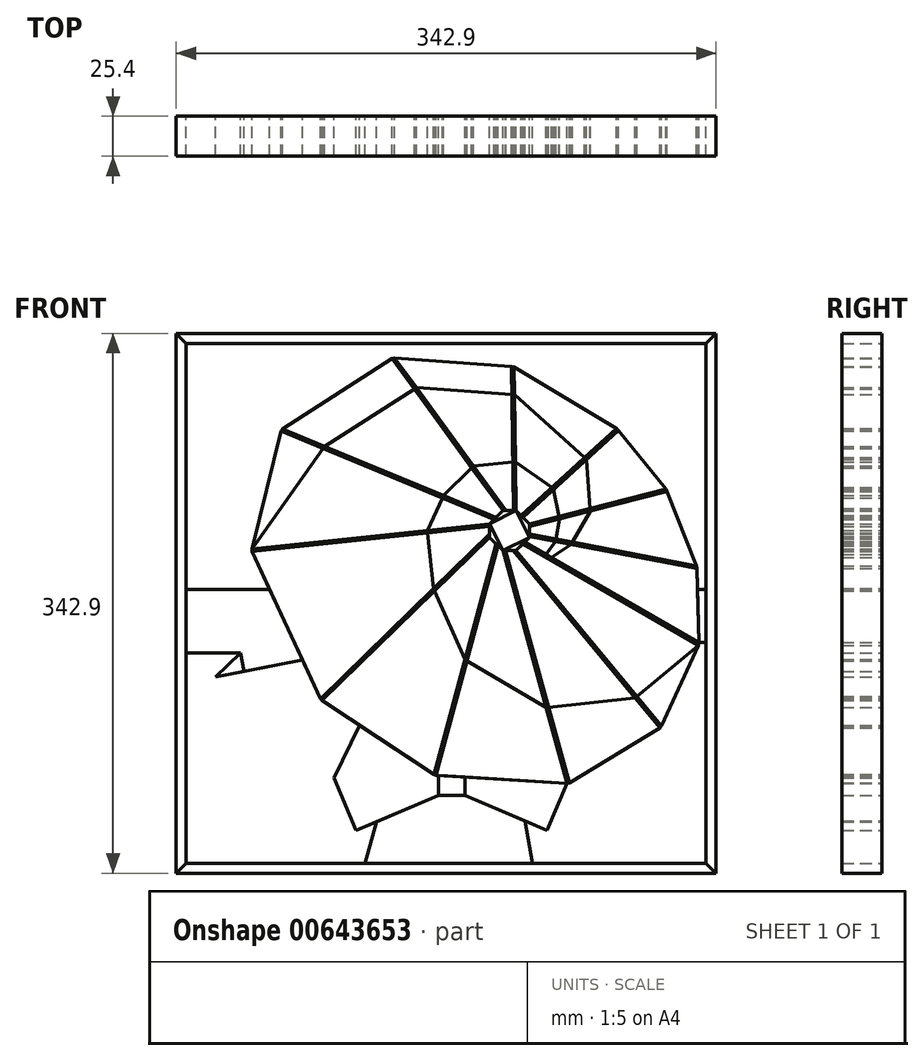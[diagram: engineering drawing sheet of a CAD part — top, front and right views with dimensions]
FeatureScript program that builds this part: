
annotation { "Feature Type Name" : "Feature", "Feature Type Description" : "" }
export const myFeature = defineFeature(function(context is Context, id is Id, definition is map)
    precondition{}
    {
        {
            var Q0;
            Q0=qCreatedBy(makeId("Front.planeOp"),FACE);
            var sketch = newSketch(context, id + "F0", { "sketchPlane" : qUnion([Q0])});
            skLineSegment(sketch, "E0.bottom", {"start": v(-171.45, 171.45) * mm, "end": v(171.45, 171.45) * mm});
            skLineSegment(sketch, "E0.top", {"start": v(-171.45, -171.45) * mm, "end": v(171.45, -171.45) * mm});
            skLineSegment(sketch, "E0.left", {"start": v(-171.45, 171.45) * mm, "end": v(-171.45, -171.45) * mm});
            skLineSegment(sketch, "E0.right", {"start": v(171.45, 171.45) * mm, "end": v(171.45, -171.45) * mm});
            skPoint(sketch, "E0.middle", {"position": v(0, 0) * mm});
            skEllipse(sketch, "E1", {"center": v(19.18, 20.15) * mm, "majorRadius": 153.05 * mm, "minorRadius": 127.05 * mm, "majorAxis": v(0.77, -0.64), "construction": true});
            skLineSegment(sketch, "E2", {"start": v(-55.07, -77.44) * mm, "end": v(-71.28, -110.8) * mm});
            skLineSegment(sketch, "E3", {"start": v(-71.28, -110.8) * mm, "end": v(-57.16, -144.18) * mm});
            skLineSegment(sketch, "E4", {"start": v(-57.16, -144.18) * mm, "end": v(-4.94, -122.09) * mm});
            skLineSegment(sketch, "E5", {"start": v(-4.94, -122.09) * mm, "end": v(-4.94, -109.66) * mm});
            skLineSegment(sketch, "E6", {"start": v(-4.94, -122.09) * mm, "end": v(11.84, -122.09) * mm});
            skLineSegment(sketch, "E7", {"start": v(11.84, -122.09) * mm, "end": v(11.84, -114.36) * mm});
            skLineSegment(sketch, "E8", {"start": v(11.84, -122.09) * mm, "end": v(64.05, -144.18) * mm});
            skLineSegment(sketch, "E9", {"start": v(64.05, -144.18) * mm, "end": v(76.64, -114.43) * mm});
            skLineSegment(sketch, "E10", {"start": v(-171.45, -34.2) * mm, "end": v(-136.3, -34.2) * mm});
            skLineSegment(sketch, "E11", {"start": v(-136.3, -34.2) * mm, "end": v(-152.24, -49.39) * mm});
            skLineSegment(sketch, "E12", {"start": v(-152.24, -49.39) * mm, "end": v(-97.01, -38.77) * mm});
            skLineSegment(sketch, "E13", {"start": v(-136.3, -34.2) * mm, "end": v(-134.05, -45.89) * mm});
            skLineSegment(sketch, "E14", {"start": v(159.43, -30.92) * mm, "end": v(171.45, -30.92) * mm});
            skLineSegment(sketch, "E15", {"start": v(-171.45, 6.09) * mm, "end": v(-118.09, 6.09) * mm});
            skLineSegment(sketch, "E16", {"start": v(171.45, 6.09) * mm, "end": v(161.71, 6.09) * mm});
            skPoint(sketch, "E17.endSnap0", {"position": v(-64.22, -127.5) * mm});
            skLineSegment(sketch, "E18", {"start": v(-44.24, -138.72) * mm, "end": v(-53.12, -171.45) * mm});
            skLineSegment(sketch, "E19", {"start": v(50.01, -138.24) * mm, "end": v(55.89, -171.45) * mm});
            skLineSegment(sketch, "E20.bottom", {"start": v(44.47, 33.4) * mm, "end": v(36, 33.4) * mm});
            skLineSegment(sketch, "E20.top", {"start": v(44.47, 58.8) * mm, "end": v(36, 58.8) * mm});
            skLineSegment(sketch, "E20.left", {"start": v(52.93, 41.87) * mm, "end": v(52.93, 50.33) * mm});
            skLineSegment(sketch, "E20.right", {"start": v(27.53, 41.87) * mm, "end": v(27.53, 50.33) * mm});
            skPoint(sketch, "E20.middle", {"position": v(41.77, 46.48) * mm});
            skLineSegment(sketch, "E21", {"start": v(44.47, 58.8) * mm, "end": v(43.1, 150.02) * mm});
            skLineSegment(sketch, "E22", {"start": v(52.93, 42.42) * mm, "end": v(159.45, 22) * mm});
            skLineSegment(sketch, "E23", {"start": v(44.47, 33.4) * mm, "end": v(136.73, -77.86) * mm});
            skLineSegment(sketch, "E24.0", {"start": v(52.93, 50.33) * mm, "end": v(139.57, 72.45) * mm});
            skLineSegment(sketch, "E25", {"start": v(27.53, 41.87) * mm, "end": v(36, 33.4) * mm});
            skLineSegment(sketch, "E26", {"start": v(27.53, 50.33) * mm, "end": v(36, 58.8) * mm});
            skLineSegment(sketch, "E27", {"start": v(44.47, 58.8) * mm, "end": v(52.93, 50.33) * mm});
            skLineSegment(sketch, "E28", {"start": v(52.93, 41.87) * mm, "end": v(44.47, 33.4) * mm});
            skLineSegment(sketch, "E29.0", {"start": v(52.93, 44.04) * mm, "end": v(159.1, 23.68) * mm});
            skLineSegment(sketch, "E30.0", {"start": v(52.93, 48.7) * mm, "end": v(140.42, 71.02) * mm});
            skPoint(sketch, "E31", {"position": v(48.7, 54.57) * mm});
            skLineSegment(sketch, "E32", {"start": v(36, 33.4) * mm, "end": v(76.64, -114.43) * mm});
            skLineSegment(sketch, "E33", {"start": v(37.65, 33.4) * mm, "end": v(78.18, -114.05) * mm});
            skLineSegment(sketch, "E34", {"start": v(76.64, -114.43) * mm, "end": v(78.18, -114.05) * mm});
            skPoint(sketch, "E35.orphan", {"position": v(78.29, -114.43) * mm});
            skLineSegment(sketch, "E36", {"start": v(42.4, 33.4) * mm, "end": v(135.68, -79.1) * mm});
            skLineSegment(sketch, "E37", {"start": v(135.68, -79.1) * mm, "end": v(136.73, -77.86) * mm});
            skPoint(sketch, "E38", {"position": v(31.77, 37.63) * mm});
            skPoint(sketch, "E39", {"position": v(31.77, 54.57) * mm});
            skPoint(sketch, "E40", {"position": v(48.7, 37.63) * mm});
            skLineSegment(sketch, "E41", {"start": v(27.53, 41.87) * mm, "end": v(-78.73, -61.81) * mm});
            skLineSegment(sketch, "E42", {"start": v(27.53, 44.09) * mm, "end": v(-79.8, -60.65) * mm});
            skLineSegment(sketch, "E43", {"start": v(-79.8, -60.65) * mm, "end": v(-78.73, -61.81) * mm});
            skLineSegment(sketch, "E44", {"start": v(27.53, 50.33) * mm, "end": v(-123.4, 34.61) * mm});
            skLineSegment(sketch, "E45", {"start": v(27.53, 48.74) * mm, "end": v(-123.25, 33.03) * mm});
            skLineSegment(sketch, "E46", {"start": v(-123.25, 33.03) * mm, "end": v(-123.4, 34.61) * mm});
            skLineSegment(sketch, "E47", {"start": v(36, 58.8) * mm, "end": v(-34.43, 155.6) * mm});
            skLineSegment(sketch, "E48", {"start": v(37.96, 58.8) * mm, "end": v(-32.71, 155.94) * mm});
            skLineSegment(sketch, "E49", {"start": v(-32.71, 155.94) * mm, "end": v(-34.43, 155.6) * mm});
            skLineSegment(sketch, "E50", {"start": v(42.88, 58.8) * mm, "end": v(41.5, 150.55) * mm});
            skLineSegment(sketch, "E51", {"start": v(41.5, 150.55) * mm, "end": v(43.1, 150.02) * mm});
            skLineSegment(sketch, "E52", {"start": v(139.57, 72.45) * mm, "end": v(140.42, 71.02) * mm});
            skLineSegment(sketch, "E53", {"start": v(159.1, 23.68) * mm, "end": v(159.45, 22) * mm});
            skLineSegment(sketch, "E54.0", {"start": v(48.92, 37.86) * mm, "end": v(160.28, -26.62) * mm});
            skLineSegment(sketch, "E55.0", {"start": v(50.08, 39.02) * mm, "end": v(160.56, -24.95) * mm});
            skLineSegment(sketch, "E56", {"start": v(160.28, -26.62) * mm, "end": v(160.56, -24.95) * mm});
            skLineSegment(sketch, "E57.0", {"start": v(30.6, 38.8) * mm, "end": v(-7.79, -108.67) * mm});
            skLineSegment(sketch, "E58.0", {"start": v(31.9, 37.5) * mm, "end": v(-6.28, -109.2) * mm});
            skLineSegment(sketch, "E59", {"start": v(-7.79, -108.67) * mm, "end": v(-6.28, -109.2) * mm});
            skLineSegment(sketch, "E60.0", {"start": v(31.44, 54.24) * mm, "end": v(-104.24, 110.44) * mm});
            skLineSegment(sketch, "E61.0", {"start": v(30.22, 53.02) * mm, "end": v(-105.15, 109.1) * mm});
            skLineSegment(sketch, "E62", {"start": v(-105.15, 109.1) * mm, "end": v(-104.24, 110.44) * mm});
            skLineSegment(sketch, "E63.0", {"start": v(48.73, 54.54) * mm, "end": v(109.36, 109.88) * mm});
            skLineSegment(sketch, "E64.0", {"start": v(47.6, 55.66) * mm, "end": v(108.2, 110.97) * mm});
            skLineSegment(sketch, "E65", {"start": v(108.2, 110.97) * mm, "end": v(109.36, 109.88) * mm});
            skPoint(sketch, "E66.start.orphan", {"position": v(78.17, -110.8) * mm});
            skLineSegment(sketch, "E67", {"start": v(-79.8, -60.65) * mm, "end": v(-123.25, 33.03) * mm});
            skLineSegment(sketch, "E68", {"start": v(-7.79, -108.67) * mm, "end": v(-78.73, -61.81) * mm});
            skLineSegment(sketch, "E69", {"start": v(-6.28, -109.2) * mm, "end": v(76.64, -114.43) * mm});
            skLineSegment(sketch, "E70", {"start": v(78.18, -114.05) * mm, "end": v(135.68, -79.1) * mm});
            skLineSegment(sketch, "E71", {"start": v(136.73, -77.86) * mm, "end": v(160.28, -26.62) * mm});
            skLineSegment(sketch, "E72", {"start": v(160.56, -24.95) * mm, "end": v(159.45, 22) * mm});
            skLineSegment(sketch, "E73", {"start": v(159.1, 23.68) * mm, "end": v(140.42, 71.02) * mm});
            skLineSegment(sketch, "E74", {"start": v(139.57, 72.45) * mm, "end": v(109.36, 109.88) * mm});
            skLineSegment(sketch, "E75", {"start": v(108.2, 110.97) * mm, "end": v(43.1, 150.02) * mm});
            skLineSegment(sketch, "E76", {"start": v(41.5, 150.55) * mm, "end": v(-32.71, 155.94) * mm});
            skLineSegment(sketch, "E77", {"start": v(-34.43, 155.6) * mm, "end": v(-104.24, 110.44) * mm});
            skLineSegment(sketch, "E78", {"start": v(-105.15, 109.1) * mm, "end": v(-123.4, 34.61) * mm});
            skLineSegment(sketch, "E79", {"start": v(-63.45, 91.83) * mm, "end": v(-69.06, 40.27) * mm});
            skLineSegment(sketch, "E80", {"start": v(-42.26, -26.23) * mm, "end": v(7.03, -51.75) * mm});
            skLineSegment(sketch, "E81", {"start": v(8.67, -51.75) * mm, "end": v(60.29, -54.95) * mm});
            skLineSegment(sketch, "E82", {"start": v(61.85, -54.65) * mm, "end": v(96.57, -31.92) * mm});
            skLineSegment(sketch, "E83", {"start": v(97.3, -30.31) * mm, "end": v(114.71, -0.24) * mm});
            skLineSegment(sketch, "E84", {"start": v(116.62, 0.5) * mm, "end": v(119.66, 29.63) * mm});
            skLineSegment(sketch, "E85", {"start": v(119.27, 31.32) * mm, "end": v(103.69, 61.65) * mm});
            skLineSegment(sketch, "E86", {"start": v(102.5, 62.99) * mm, "end": v(76.55, 79.93) * mm});
            skLineSegment(sketch, "E87", {"start": v(74.91, 80.59) * mm, "end": v(44.04, 87.04) * mm});
            skLineSegment(sketch, "E88", {"start": v(42.45, 87.4) * mm, "end": v(23.02, 79.33) * mm});
            skLineSegment(sketch, "E89", {"start": v(22.08, 77.93) * mm, "end": v(12.86, 61.94) * mm});
            skLineSegment(sketch, "E90", {"start": v(12.62, 60.32) * mm, "end": v(13.77, 48.9) * mm});
            skLineSegment(sketch, "E91", {"start": v(13.77, 48.9) * mm, "end": v(19.14, 35.9) * mm});
            skLineSegment(sketch, "E92", {"start": v(20.27, 34.78) * mm, "end": v(28.24, 29.73) * mm});
            skLineSegment(sketch, "E93", {"start": v(29.53, 28.39) * mm, "end": v(37.38, 28.39) * mm});
            skLineSegment(sketch, "E94", {"start": v(39.12, 28.04) * mm, "end": v(45.41, 29.77) * mm});
            skLineSegment(sketch, "E95", {"start": v(47, 30.34) * mm, "end": v(52.79, 35.62) * mm});
            skLineSegment(sketch, "E96", {"start": v(53.8, 36.87) * mm, "end": v(56.61, 41.72) * mm});
            skLineSegment(sketch, "E97", {"start": v(57, 43.26) * mm, "end": v(52.93, 48.7) * mm});
            skLineSegment(sketch, "E98", {"start": v(-16.6, 131.1) * mm, "end": v(-62.47, 93.14) * mm});
            skLineSegment(sketch, "E99", {"start": v(-69, 38.68) * mm, "end": v(-43.22, -24.95) * mm});
            skLineSegment(sketch, "E100", {"start": v(-15.61, 132.44) * mm, "end": v(41.62, 143.24) * mm});
            skLineSegment(sketch, "E101", {"start": v(43.2, 143.24) * mm, "end": v(108.2, 110.97) * mm});
            skLineSegment(sketch, "E102", {"start": v(44.47, 58.8) * mm, "end": v(52.93, 41.87) * mm});
            skLineSegment(sketch, "E103", {"start": v(52.93, 41.87) * mm, "end": v(36, 33.4) * mm});
            skLineSegment(sketch, "E104", {"start": v(36, 33.4) * mm, "end": v(27.53, 50.33) * mm});
            skLineSegment(sketch, "E105", {"start": v(27.53, 50.33) * mm, "end": v(44.47, 58.8) * mm});
            skLineSegment(sketch, "E106.bottom", {"start": v(227.62, -554.84) * mm, "end": v(570.52, -554.84) * mm});
            skLineSegment(sketch, "E106.top", {"start": v(227.62, -897.74) * mm, "end": v(570.52, -897.74) * mm});
            skLineSegment(sketch, "E106.left", {"start": v(227.62, -554.84) * mm, "end": v(227.62, -897.74) * mm});
            skLineSegment(sketch, "E106.right", {"start": v(570.52, -554.84) * mm, "end": v(570.52, -897.74) * mm});
            skEllipse(sketch, "E107", {"center": v(418.25, -706.14) * mm, "majorRadius": 153.05 * mm, "minorRadius": 127.05 * mm, "majorAxis": v(0.77, -0.64), "construction": true});
            skLineSegment(sketch, "E108", {"start": v(344, -803.73) * mm, "end": v(327.79, -837.09) * mm});
            skLineSegment(sketch, "E109", {"start": v(327.79, -837.09) * mm, "end": v(341.91, -870.47) * mm});
            skLineSegment(sketch, "E110", {"start": v(341.91, -870.47) * mm, "end": v(394.13, -848.37) * mm});
            skLineSegment(sketch, "E111", {"start": v(394.13, -848.37) * mm, "end": v(394.13, -835.57) * mm});
            skLineSegment(sketch, "E112", {"start": v(394.13, -848.37) * mm, "end": v(410.9, -848.37) * mm});
            skLineSegment(sketch, "E113", {"start": v(410.9, -848.37) * mm, "end": v(410.9, -836.63) * mm});
            skLineSegment(sketch, "E114", {"start": v(410.9, -848.37) * mm, "end": v(463.12, -870.47) * mm});
            skLineSegment(sketch, "E115", {"start": v(463.12, -870.47) * mm, "end": v(475.7, -840.72) * mm});
            skLineSegment(sketch, "E116", {"start": v(233.97, -757.8) * mm, "end": v(268.58, -757.8) * mm});
            skLineSegment(sketch, "E117", {"start": v(268.58, -757.8) * mm, "end": v(252.63, -772.98) * mm});
            skLineSegment(sketch, "E118", {"start": v(252.63, -772.98) * mm, "end": v(307.86, -762.36) * mm});
            skLineSegment(sketch, "E119", {"start": v(268.58, -757.8) * mm, "end": v(270.83, -769.48) * mm});
            skLineSegment(sketch, "E120", {"start": v(559.63, -751.24) * mm, "end": v(564.17, -751.24) * mm});
            skLineSegment(sketch, "E121", {"start": v(233.97, -717.4) * mm, "end": v(287.01, -717.4) * mm});
            skLineSegment(sketch, "E122", {"start": v(564.17, -717.4) * mm, "end": v(558.83, -717.4) * mm});
            skPoint(sketch, "E123.endSnap0", {"position": v(334.85, -853.78) * mm});
            skLineSegment(sketch, "E124", {"start": v(354.83, -865) * mm, "end": v(347.67, -891.39) * mm});
            skLineSegment(sketch, "E125", {"start": v(449.08, -864.53) * mm, "end": v(453.83, -891.39) * mm});
            skLineSegment(sketch, "E126.bottom", {"start": v(443.53, -692.89) * mm, "end": v(435.07, -692.89) * mm});
            skLineSegment(sketch, "E126.top", {"start": v(443.53, -667.49) * mm, "end": v(435.07, -667.49) * mm});
            skLineSegment(sketch, "E126.left", {"start": v(452, -684.42) * mm, "end": v(452, -675.95) * mm});
            skLineSegment(sketch, "E126.right", {"start": v(426.6, -684.42) * mm, "end": v(426.6, -675.95) * mm});
            skPoint(sketch, "E126.middle", {"position": v(440.83, -679.8) * mm});
            skLineSegment(sketch, "E127", {"start": v(443.53, -667.49) * mm, "end": v(442.17, -576.27) * mm});
            skLineSegment(sketch, "E128", {"start": v(452, -683.86) * mm, "end": v(558.52, -704.29) * mm});
            skLineSegment(sketch, "E129", {"start": v(443.53, -692.89) * mm, "end": v(535.8, -804.15) * mm});
            skLineSegment(sketch, "E130.0", {"start": v(452, -675.95) * mm, "end": v(538.59, -653.76) * mm});
            skLineSegment(sketch, "E131", {"start": v(426.6, -684.42) * mm, "end": v(435.07, -692.89) * mm});
            skLineSegment(sketch, "E132", {"start": v(426.6, -675.95) * mm, "end": v(435.07, -667.49) * mm});
            skLineSegment(sketch, "E133", {"start": v(443.53, -667.49) * mm, "end": v(452, -675.95) * mm});
            skLineSegment(sketch, "E134", {"start": v(452, -684.42) * mm, "end": v(443.53, -692.89) * mm});
            skLineSegment(sketch, "E135.0", {"start": v(452, -682.25) * mm, "end": v(558.17, -702.6) * mm});
            skLineSegment(sketch, "E136.0", {"start": v(452, -677.6) * mm, "end": v(539.43, -655.18) * mm});
            skPoint(sketch, "E137", {"position": v(447.77, -671.72) * mm});
            skLineSegment(sketch, "E138", {"start": v(435.07, -692.89) * mm, "end": v(475.7, -840.72) * mm});
            skLineSegment(sketch, "E139", {"start": v(436.71, -692.89) * mm, "end": v(477.25, -840.34) * mm});
            skLineSegment(sketch, "E140", {"start": v(475.7, -840.72) * mm, "end": v(477.25, -840.34) * mm});
            skPoint(sketch, "E141.orphan", {"position": v(477.35, -840.72) * mm});
            skLineSegment(sketch, "E142", {"start": v(441.47, -692.89) * mm, "end": v(534.75, -805.38) * mm});
            skLineSegment(sketch, "E143", {"start": v(534.75, -805.38) * mm, "end": v(535.8, -804.15) * mm});
            skPoint(sketch, "E144", {"position": v(430.83, -688.65) * mm});
            skPoint(sketch, "E145", {"position": v(430.83, -671.72) * mm});
            skPoint(sketch, "E146", {"position": v(447.77, -688.65) * mm});
            skLineSegment(sketch, "E147", {"start": v(426.6, -684.42) * mm, "end": v(320.34, -788.1) * mm});
            skLineSegment(sketch, "E148", {"start": v(426.6, -682.2) * mm, "end": v(319.26, -786.94) * mm});
            skLineSegment(sketch, "E149", {"start": v(319.26, -786.94) * mm, "end": v(320.34, -788.1) * mm});
            skLineSegment(sketch, "E150", {"start": v(426.6, -675.95) * mm, "end": v(275.68, -691.67) * mm});
            skLineSegment(sketch, "E151", {"start": v(426.6, -677.55) * mm, "end": v(275.81, -693.25) * mm});
            skLineSegment(sketch, "E152", {"start": v(275.81, -693.25) * mm, "end": v(275.68, -691.67) * mm});
            skLineSegment(sketch, "E153", {"start": v(435.07, -667.49) * mm, "end": v(364.64, -570.69) * mm});
            skLineSegment(sketch, "E154", {"start": v(437.03, -667.49) * mm, "end": v(366.35, -570.34) * mm});
            skLineSegment(sketch, "E155", {"start": v(366.35, -570.34) * mm, "end": v(364.64, -570.69) * mm});
            skLineSegment(sketch, "E156", {"start": v(441.94, -667.49) * mm, "end": v(440.57, -575.74) * mm});
            skLineSegment(sketch, "E157", {"start": v(440.57, -575.74) * mm, "end": v(442.17, -576.27) * mm});
            skLineSegment(sketch, "E158", {"start": v(538.59, -653.76) * mm, "end": v(539.43, -655.18) * mm});
            skLineSegment(sketch, "E159", {"start": v(558.17, -702.6) * mm, "end": v(558.52, -704.29) * mm});
            skLineSegment(sketch, "E160.0", {"start": v(447.77, -688.65) * mm, "end": v(559.35, -752.9) * mm});
            skLineSegment(sketch, "E161.0", {"start": v(448.93, -687.49) * mm, "end": v(559.63, -751.24) * mm});
            skLineSegment(sketch, "E162", {"start": v(559.35, -752.9) * mm, "end": v(559.63, -751.24) * mm});
            skLineSegment(sketch, "E163.0", {"start": v(430.83, -688.65) * mm, "end": v(391.28, -834.95) * mm});
            skLineSegment(sketch, "E164.0", {"start": v(432.13, -689.95) * mm, "end": v(392.78, -835.48) * mm});
            skLineSegment(sketch, "E165", {"start": v(391.28, -834.95) * mm, "end": v(392.78, -835.48) * mm});
            skLineSegment(sketch, "E166.0", {"start": v(430.83, -671.72) * mm, "end": v(295.08, -615.49) * mm});
            skLineSegment(sketch, "E167.0", {"start": v(429.62, -672.93) * mm, "end": v(294.16, -616.82) * mm});
            skLineSegment(sketch, "E168", {"start": v(294.16, -616.82) * mm, "end": v(295.08, -615.49) * mm});
            skLineSegment(sketch, "E169.0", {"start": v(447.8, -671.75) * mm, "end": v(508.43, -616.4) * mm});
            skLineSegment(sketch, "E170.0", {"start": v(446.67, -670.62) * mm, "end": v(507.27, -615.31) * mm});
            skLineSegment(sketch, "E171", {"start": v(507.27, -615.31) * mm, "end": v(508.43, -616.4) * mm});
            skPoint(sketch, "E172.start.orphan", {"position": v(477.24, -837.09) * mm});
            skLineSegment(sketch, "E173", {"start": v(319.26, -786.94) * mm, "end": v(275.81, -693.25) * mm});
            skLineSegment(sketch, "E174", {"start": v(391.28, -834.95) * mm, "end": v(320.34, -788.1) * mm});
            skLineSegment(sketch, "E175", {"start": v(392.78, -835.48) * mm, "end": v(475.7, -840.72) * mm});
            skLineSegment(sketch, "E176", {"start": v(477.25, -840.34) * mm, "end": v(534.75, -805.38) * mm});
            skLineSegment(sketch, "E177", {"start": v(535.8, -804.15) * mm, "end": v(559.35, -752.9) * mm});
            skLineSegment(sketch, "E178", {"start": v(559.63, -751.24) * mm, "end": v(558.52, -704.29) * mm});
            skLineSegment(sketch, "E179", {"start": v(558.17, -702.6) * mm, "end": v(539.43, -655.18) * mm});
            skLineSegment(sketch, "E180", {"start": v(538.59, -653.76) * mm, "end": v(508.43, -616.4) * mm});
            skLineSegment(sketch, "E181", {"start": v(507.27, -615.31) * mm, "end": v(442.17, -576.27) * mm});
            skLineSegment(sketch, "E182", {"start": v(440.57, -575.74) * mm, "end": v(366.35, -570.34) * mm});
            skLineSegment(sketch, "E183", {"start": v(364.64, -570.69) * mm, "end": v(295.08, -615.49) * mm});
            skLineSegment(sketch, "E184", {"start": v(294.16, -616.82) * mm, "end": v(275.68, -691.67) * mm});
            skLineSegment(sketch, "E185", {"start": v(443.53, -667.49) * mm, "end": v(452, -684.42) * mm});
            skLineSegment(sketch, "E186", {"start": v(452, -684.42) * mm, "end": v(435.07, -692.89) * mm});
            skLineSegment(sketch, "E187", {"start": v(435.07, -692.89) * mm, "end": v(426.6, -675.95) * mm});
            skLineSegment(sketch, "E188", {"start": v(426.6, -675.95) * mm, "end": v(443.53, -667.49) * mm});
            skLineSegment(sketch, "E189.bottom", {"start": v(-908.02, -312.88) * mm, "end": v(-565.12, -312.88) * mm});
            skLineSegment(sketch, "E189.top", {"start": v(-908.02, -655.78) * mm, "end": v(-565.12, -655.78) * mm});
            skLineSegment(sketch, "E189.left", {"start": v(-908.02, -312.88) * mm, "end": v(-908.02, -655.78) * mm});
            skLineSegment(sketch, "E189.right", {"start": v(-565.12, -312.88) * mm, "end": v(-565.12, -655.78) * mm});
            skPoint(sketch, "E189.middle", {"position": v(-736.57, -484.33) * mm});
            skEllipse(sketch, "E190", {"center": v(-717.4, -464.18) * mm, "majorRadius": 153.05 * mm, "minorRadius": 127.05 * mm, "majorAxis": v(0.77, -0.64), "construction": true});
            skLineSegment(sketch, "E191", {"start": v(-791.64, -561.77) * mm, "end": v(-807.85, -595.14) * mm});
            skLineSegment(sketch, "E192", {"start": v(-807.85, -595.14) * mm, "end": v(-793.73, -628.51) * mm});
            skLineSegment(sketch, "E193", {"start": v(-793.73, -628.51) * mm, "end": v(-741.51, -606.42) * mm});
            skLineSegment(sketch, "E194", {"start": v(-741.51, -606.42) * mm, "end": v(-741.51, -593.99) * mm});
            skLineSegment(sketch, "E195", {"start": v(-741.51, -606.42) * mm, "end": v(-724.74, -606.42) * mm});
            skLineSegment(sketch, "E196", {"start": v(-724.74, -606.42) * mm, "end": v(-724.74, -598.7) * mm});
            skLineSegment(sketch, "E197", {"start": v(-724.74, -606.42) * mm, "end": v(-672.52, -628.51) * mm});
            skLineSegment(sketch, "E198", {"start": v(-672.52, -628.51) * mm, "end": v(-659.93, -598.76) * mm});
            skLineSegment(sketch, "E199", {"start": v(-908.02, -518.53) * mm, "end": v(-872.87, -518.53) * mm});
            skLineSegment(sketch, "E200", {"start": v(-872.87, -518.53) * mm, "end": v(-888.81, -533.72) * mm});
            skLineSegment(sketch, "E201", {"start": v(-888.81, -533.72) * mm, "end": v(-833.58, -523.1) * mm});
            skLineSegment(sketch, "E202", {"start": v(-872.87, -518.53) * mm, "end": v(-870.62, -530.22) * mm});
            skLineSegment(sketch, "E203", {"start": v(-577.14, -515.25) * mm, "end": v(-565.12, -515.25) * mm});
            skLineSegment(sketch, "E204", {"start": v(-908.02, -478.25) * mm, "end": v(-854.66, -478.25) * mm});
            skLineSegment(sketch, "E205", {"start": v(-565.12, -478.25) * mm, "end": v(-574.86, -478.25) * mm});
            skPoint(sketch, "E206.endSnap0", {"position": v(-800.79, -611.82) * mm});
            skLineSegment(sketch, "E207", {"start": v(-780.8, -623.05) * mm, "end": v(-789.7, -655.78) * mm});
            skLineSegment(sketch, "E208", {"start": v(-686.56, -622.57) * mm, "end": v(-680.69, -655.78) * mm});
            skLineSegment(sketch, "E209.bottom", {"start": v(-692.1, -450.93) * mm, "end": v(-700.57, -450.93) * mm});
            skLineSegment(sketch, "E209.top", {"start": v(-692.1, -425.53) * mm, "end": v(-700.57, -425.53) * mm});
            skLineSegment(sketch, "E209.left", {"start": v(-683.64, -442.46) * mm, "end": v(-683.64, -434) * mm});
            skLineSegment(sketch, "E209.right", {"start": v(-709.04, -442.46) * mm, "end": v(-709.04, -434) * mm});
            skPoint(sketch, "E209.middle", {"position": v(-694.8, -437.85) * mm});
            skLineSegment(sketch, "E210", {"start": v(-692.1, -425.53) * mm, "end": v(-693.47, -334.31) * mm});
            skLineSegment(sketch, "E211", {"start": v(-683.64, -441.91) * mm, "end": v(-577.12, -462.33) * mm});
            skLineSegment(sketch, "E212", {"start": v(-692.1, -450.93) * mm, "end": v(-599.84, -562.2) * mm});
            skLineSegment(sketch, "E213.0", {"start": v(-683.64, -434) * mm, "end": v(-597, -411.89) * mm});
            skLineSegment(sketch, "E214", {"start": v(-709.04, -442.46) * mm, "end": v(-700.57, -450.93) * mm});
            skLineSegment(sketch, "E215", {"start": v(-709.04, -434) * mm, "end": v(-700.57, -425.53) * mm});
            skLineSegment(sketch, "E216", {"start": v(-692.1, -425.53) * mm, "end": v(-683.64, -434) * mm});
            skLineSegment(sketch, "E217", {"start": v(-683.64, -442.46) * mm, "end": v(-692.1, -450.93) * mm});
            skLineSegment(sketch, "E218.0", {"start": v(-683.64, -440.3) * mm, "end": v(-577.47, -460.65) * mm});
            skLineSegment(sketch, "E219.0", {"start": v(-683.64, -435.64) * mm, "end": v(-596.16, -413.3) * mm});
            skPoint(sketch, "E220", {"position": v(-687.87, -429.76) * mm});
            skLineSegment(sketch, "E221", {"start": v(-700.57, -450.93) * mm, "end": v(-659.93, -598.76) * mm});
            skLineSegment(sketch, "E222", {"start": v(-698.93, -450.93) * mm, "end": v(-658.39, -598.39) * mm});
            skLineSegment(sketch, "E223", {"start": v(-659.93, -598.76) * mm, "end": v(-658.39, -598.39) * mm});
            skPoint(sketch, "E224.orphan", {"position": v(-658.28, -598.76) * mm});
            skLineSegment(sketch, "E225", {"start": v(-694.17, -450.93) * mm, "end": v(-600.89, -563.42) * mm});
            skLineSegment(sketch, "E226", {"start": v(-600.89, -563.42) * mm, "end": v(-599.84, -562.2) * mm});
            skPoint(sketch, "E227", {"position": v(-704.8, -446.7) * mm});
            skPoint(sketch, "E228", {"position": v(-704.8, -429.76) * mm});
            skPoint(sketch, "E229", {"position": v(-687.87, -446.7) * mm});
            skLineSegment(sketch, "E230", {"start": v(-709.04, -442.46) * mm, "end": v(-815.3, -546.15) * mm});
            skLineSegment(sketch, "E231", {"start": v(-709.04, -440.25) * mm, "end": v(-816.38, -544.98) * mm});
            skLineSegment(sketch, "E232", {"start": v(-816.38, -544.98) * mm, "end": v(-815.3, -546.15) * mm});
            skLineSegment(sketch, "E233", {"start": v(-709.04, -434) * mm, "end": v(-859.96, -449.72) * mm});
            skLineSegment(sketch, "E234", {"start": v(-709.04, -435.6) * mm, "end": v(-859.83, -451.3) * mm});
            skLineSegment(sketch, "E235", {"start": v(-859.83, -451.3) * mm, "end": v(-859.96, -449.72) * mm});
            skLineSegment(sketch, "E236", {"start": v(-700.57, -425.53) * mm, "end": v(-771, -328.73) * mm});
            skLineSegment(sketch, "E237", {"start": v(-698.6, -425.53) * mm, "end": v(-769.29, -328.39) * mm});
            skLineSegment(sketch, "E238", {"start": v(-769.29, -328.39) * mm, "end": v(-771, -328.73) * mm});
            skLineSegment(sketch, "E239", {"start": v(-693.7, -425.53) * mm, "end": v(-695.06, -333.78) * mm});
            skLineSegment(sketch, "E240", {"start": v(-695.06, -333.78) * mm, "end": v(-693.47, -334.31) * mm});
            skLineSegment(sketch, "E241", {"start": v(-597, -411.89) * mm, "end": v(-596.16, -413.3) * mm});
            skLineSegment(sketch, "E242", {"start": v(-577.47, -460.65) * mm, "end": v(-577.12, -462.33) * mm});
            skLineSegment(sketch, "E243.0", {"start": v(-687.65, -446.47) * mm, "end": v(-576.3, -510.95) * mm});
            skLineSegment(sketch, "E244.0", {"start": v(-686.49, -445.31) * mm, "end": v(-576, -509.28) * mm});
            skLineSegment(sketch, "E245", {"start": v(-576.3, -510.95) * mm, "end": v(-576, -509.28) * mm});
            skLineSegment(sketch, "E246.0", {"start": v(-705.97, -445.53) * mm, "end": v(-744.36, -593) * mm});
            skLineSegment(sketch, "E247.0", {"start": v(-704.67, -446.84) * mm, "end": v(-742.86, -593.53) * mm});
            skLineSegment(sketch, "E248", {"start": v(-744.36, -593) * mm, "end": v(-742.86, -593.53) * mm});
            skLineSegment(sketch, "E249.0", {"start": v(-705.13, -430.1) * mm, "end": v(-840.8, -373.9) * mm});
            skLineSegment(sketch, "E250.0", {"start": v(-706.35, -431.3) * mm, "end": v(-841.72, -375.23) * mm});
            skLineSegment(sketch, "E251", {"start": v(-841.72, -375.23) * mm, "end": v(-840.8, -373.9) * mm});
            skLineSegment(sketch, "E252.0", {"start": v(-687.84, -429.8) * mm, "end": v(-627.2, -374.45) * mm});
            skLineSegment(sketch, "E253.0", {"start": v(-688.97, -428.67) * mm, "end": v(-628.37, -373.36) * mm});
            skLineSegment(sketch, "E254", {"start": v(-628.37, -373.36) * mm, "end": v(-627.2, -374.45) * mm});
            skPoint(sketch, "E255.start.orphan", {"position": v(-658.4, -595.14) * mm});
            skLineSegment(sketch, "E256", {"start": v(-816.38, -544.98) * mm, "end": v(-859.83, -451.3) * mm});
            skLineSegment(sketch, "E257", {"start": v(-744.36, -593) * mm, "end": v(-815.3, -546.15) * mm});
            skLineSegment(sketch, "E258", {"start": v(-742.86, -593.53) * mm, "end": v(-659.93, -598.76) * mm});
            skLineSegment(sketch, "E259", {"start": v(-658.39, -598.39) * mm, "end": v(-600.89, -563.42) * mm});
            skLineSegment(sketch, "E260", {"start": v(-599.84, -562.2) * mm, "end": v(-576.3, -510.95) * mm});
            skLineSegment(sketch, "E261", {"start": v(-576, -509.28) * mm, "end": v(-577.12, -462.33) * mm});
            skLineSegment(sketch, "E262", {"start": v(-577.47, -460.65) * mm, "end": v(-596.16, -413.3) * mm});
            skLineSegment(sketch, "E263", {"start": v(-597, -411.89) * mm, "end": v(-627.2, -374.45) * mm});
            skLineSegment(sketch, "E264", {"start": v(-628.37, -373.36) * mm, "end": v(-693.47, -334.31) * mm});
            skLineSegment(sketch, "E265", {"start": v(-695.06, -333.78) * mm, "end": v(-769.29, -328.39) * mm});
            skLineSegment(sketch, "E266", {"start": v(-771, -328.73) * mm, "end": v(-840.8, -373.9) * mm});
            skLineSegment(sketch, "E267", {"start": v(-841.72, -375.23) * mm, "end": v(-859.96, -449.72) * mm});
            skLineSegment(sketch, "E268", {"start": v(-692.1, -425.53) * mm, "end": v(-683.64, -442.46) * mm});
            skLineSegment(sketch, "E269", {"start": v(-683.64, -442.46) * mm, "end": v(-700.57, -450.93) * mm});
            skLineSegment(sketch, "E270", {"start": v(-700.57, -450.93) * mm, "end": v(-709.04, -434) * mm});
            skLineSegment(sketch, "E271", {"start": v(-709.04, -434) * mm, "end": v(-692.1, -425.53) * mm});
            skLineSegment(sketch, "E272", {"start": v(378.86, -590.23) * mm, "end": v(321.8, -626.56) * mm});
            skLineSegment(sketch, "E273", {"start": v(380.2, -589.38) * mm, "end": v(440.84, -593.72) * mm});
            skLineSegment(sketch, "E274", {"start": v(559.35, -752.9) * mm, "end": v(520.21, -785.36) * mm});
            skPoint(sketch, "E275.endSnap0", {"position": v(495.3, -664.86) * mm});
            skLineSegment(sketch, "E276", {"start": v(391.7, -718.47) * mm, "end": v(411.06, -761.8) * mm});
            skLineSegment(sketch, "E277", {"start": v(391, -716.93) * mm, "end": v(387.33, -681.64) * mm});
            skLineSegment(sketch, "E278", {"start": v(397.37, -657.86) * mm, "end": v(415.32, -640.35) * mm});
            skLineSegment(sketch, "E279", {"start": v(416.47, -639.23) * mm, "end": v(441.48, -636.62) * mm});
            skLineSegment(sketch, "E280", {"start": v(471.16, -672.68) * mm, "end": v(468.71, -685.45) * mm});
            skLineSegment(sketch, "E281", {"start": v(468.41, -687.01) * mm, "end": v(462.42, -695.26) * mm});
            skLineSegment(sketch, "E282", {"start": v(465.82, -697.22) * mm, "end": v(478.41, -688.93) * mm});
            skLineSegment(sketch, "E283", {"start": v(479.25, -687.47) * mm, "end": v(490.65, -667.68) * mm});
            skLineSegment(sketch, "E284", {"start": v(442.43, -593.72) * mm, "end": v(487.05, -633.77) * mm});
            skLineSegment(sketch, "E285", {"start": v(488.2, -634.87) * mm, "end": v(490.54, -666.07) * mm});
            skLineSegment(sketch, "E286", {"start": v(387.27, -680.05) * mm, "end": v(396.77, -659.33) * mm});
            skLineSegment(sketch, "E287", {"start": v(443.07, -636.62) * mm, "end": v(466.14, -652.85) * mm});
            skLineSegment(sketch, "E288", {"start": v(467.39, -653.86) * mm, "end": v(470.77, -671.14) * mm});
            skLineSegment(sketch, "E289", {"start": v(462.41, -792.35) * mm, "end": v(412.37, -763.04) * mm});
            skLineSegment(sketch, "E290", {"start": v(464.06, -792.35) * mm, "end": v(518.9, -786.26) * mm});
            skLineSegment(sketch, "E291", {"start": v(275.68, -691.67) * mm, "end": v(320.88, -627.9) * mm});
            skLineSegment(sketch, "E292.0", {"start": v(233.97, -561.19) * mm, "end": v(564.17, -561.19) * mm});
            skLineSegment(sketch, "E292.1", {"start": v(233.97, -561.19) * mm, "end": v(233.97, -891.39) * mm});
            skLineSegment(sketch, "E292.2", {"start": v(233.97, -891.39) * mm, "end": v(564.17, -891.39) * mm});
            skLineSegment(sketch, "E292.3", {"start": v(564.17, -561.19) * mm, "end": v(564.17, -891.39) * mm});
            skPoint(sketch, "E293.orphan", {"position": v(570.52, -717.4) * mm});
            skLineSegment(sketch, "E294", {"start": v(564.17, -561.19) * mm, "end": v(570.52, -554.84) * mm});
            skLineSegment(sketch, "E295", {"start": v(233.97, -891.39) * mm, "end": v(227.62, -897.74) * mm});
            skLineSegment(sketch, "E296", {"start": v(564.17, -891.39) * mm, "end": v(570.52, -897.74) * mm});
            skLineSegment(sketch, "E297", {"start": v(233.97, -561.19) * mm, "end": v(227.62, -554.84) * mm});
            skSolve(sketch);
        }
        {
            var Q0;
            {var subQ0=sQuery(id+"F0.wireOp",EDGE,"E121");Q0=makeQuery(id+"F0.imprint","IMPRINT",FACE,{"disambiguationData":[TD([[makeQuery(id+"F0.imprint","IMPRINT",EDGE,{"derivedFrom":subQ0}),1.0]])]});}
            var Q1;
            {var subQ12=sQuery(id+"F0.wireOp",EDGE,"E108");Q1=makeQuery(id+"F0.imprint","IMPRINT",FACE,{"disambiguationData":[TD([[makeQuery(id+"F0.imprint","IMPRINT",EDGE,{"derivedFrom":subQ12}),-1.0]])]});}
            var Q2;
            {var subQ5=sQuery(id+"F0.wireOp",EDGE,"E115");Q2=makeQuery(id+"F0.imprint","IMPRINT",FACE,{"disambiguationData":[TD([[makeQuery(id+"F0.imprint","IMPRINT",EDGE,{"derivedFrom":subQ5}),-1.0]])]});}
            extrude(context, id + "F1", {"entities" : qUnion([Q0, Q1, Q2]), "depth" : 25.4 * mm, "offsetDistance" : 25.4 * mm});
        }
        {
            var Q0;
            {var subQ5=sQuery(id+"F0.wireOp",EDGE,"E116");Q0=makeQuery(id+"F0.imprint","IMPRINT",FACE,{"disambiguationData":[TD([[makeQuery(id+"F0.imprint","IMPRINT",EDGE,{"derivedFrom":subQ5}),1.0]])]});}
            var Q1;
            {var subQ0=sQuery(id+"F0.wireOp",EDGE,"E120");Q1=makeQuery(id+"F0.imprint","IMPRINT",FACE,{"disambiguationData":[TD([[makeQuery(id+"F0.imprint","IMPRINT",EDGE,{"derivedFrom":subQ0}),1.0]])]});}
            extrude(context, id + "F2", {"entities" : qUnion([Q0, Q1]), "depth" : 25.4 * mm, "offsetDistance" : 25.4 * mm});
        }
        {
            var Q0;
            {var subQ0=sQuery(id+"F0.wireOp",EDGE,"E117");Q0=makeQuery(id+"F0.imprint","IMPRINT",FACE,{"disambiguationData":[TD([[makeQuery(id+"F0.imprint","IMPRINT",EDGE,{"derivedFrom":subQ0}),1.0]])]});}
            extrude(context, id + "F3", {"entities" : qUnion([Q0]), "depth" : 25.4 * mm, "offsetDistance" : 25.4 * mm});
        }
        {
            var Q0;
            {var subQ1=sQuery(id+"F0.wireOp",EDGE,"E112");Q0=makeQuery(id+"F0.imprint","IMPRINT",FACE,{"disambiguationData":[TD([[makeQuery(id+"F0.imprint","IMPRINT",EDGE,{"derivedFrom":subQ1}),-1.0]])]});}
            extrude(context, id + "F4", {"entities" : qUnion([Q0]), "depth" : 25.4 * mm, "offsetDistance" : 25.4 * mm});
        }
        {
            var Q0;
            {var subQ6=sQuery(id+"F0.wireOp",EDGE,"E108");Q0=makeQuery(id+"F0.imprint","IMPRINT",FACE,{"disambiguationData":[TD([[makeQuery(id+"F0.imprint","IMPRINT",EDGE,{"derivedFrom":subQ6}),1.0]])]});}
            var Q1;
            {var subQ3=sQuery(id+"F0.wireOp",EDGE,"E113");Q1=makeQuery(id+"F0.imprint","IMPRINT",FACE,{"disambiguationData":[TD([[makeQuery(id+"F0.imprint","IMPRINT",EDGE,{"derivedFrom":subQ3}),-1.0]])]});}
            extrude(context, id + "F5", {"entities" : qUnion([Q0, Q1]), "depth" : 25.4 * mm, "offsetDistance" : 25.4 * mm});
        }
        {
            var Q0;
            {var subQ0=sQuery(id+"F0.wireOp",EDGE,"E111");Q0=makeQuery(id+"F0.imprint","IMPRINT",FACE,{"disambiguationData":[TD([[makeQuery(id+"F0.imprint","IMPRINT",EDGE,{"derivedFrom":subQ0}),-1.0]])]});}
            var Q1;
            Q1=makeQuery(id+"F0.imprint","IMPRINT",FACE,{"disambiguationData":[TD([[makeQuery(id+"F0.imprint","IMPRINT",EDGE,{"derivedFrom":sQuery(id+"F0.wireOp",EDGE,"E106.top")}),1.0]])]});
            var Q2;
            Q2=makeQuery(id+"F0.imprint","IMPRINT",FACE,{"disambiguationData":[TD([[makeQuery(id+"F0.imprint","IMPRINT",EDGE,{"derivedFrom":sQuery(id+"F0.wireOp",EDGE,"E106.bottom")}),-1.0]])]});
            extrude(context, id + "F6", {"entities" : qUnion([Q0, Q1, Q2]), "depth" : 25.4 * mm, "offsetDistance" : 25.4 * mm});
        }
        {
            var Q0;
            Q0=makeQuery(id+"F0.imprint","IMPRINT",FACE,{"disambiguationData":[TD([[makeQuery(id+"F0.imprint","IMPRINT",EDGE,{"derivedFrom":sQuery(id+"F0.wireOp",EDGE,"E106.left")}),1.0]])]});
            var Q1;
            Q1=makeQuery(id+"F0.imprint","IMPRINT",FACE,{"disambiguationData":[TD([[makeQuery(id+"F0.imprint","IMPRINT",EDGE,{"derivedFrom":sQuery(id+"F0.wireOp",EDGE,"E106.right")}),-1.0]])]});
            extrude(context, id + "F7", {"entities" : qUnion([Q0, Q1]), "depth" : 25.4 * mm, "offsetDistance" : 25.4 * mm});
        }
        {
            var Q0;
            {var subQ0=sQuery(id+"F0.wireOp",EDGE,"E184");Q0=makeQuery(id+"F0.imprint","IMPRINT",FACE,{"disambiguationData":[TD([[makeQuery(id+"F0.imprint","IMPRINT",EDGE,{"derivedFrom":subQ0}),1.0]])]});}
            var Q1;
            {var subQ0=sQuery(id+"F0.wireOp",EDGE,"E183");Q1=makeQuery(id+"F0.imprint","IMPRINT",FACE,{"disambiguationData":[TD([[makeQuery(id+"F0.imprint","IMPRINT",EDGE,{"derivedFrom":subQ0}),1.0]])]});}
            var Q2;
            {var subQ0=sQuery(id+"F0.wireOp",EDGE,"E182");Q2=makeQuery(id+"F0.imprint","IMPRINT",FACE,{"disambiguationData":[TD([[makeQuery(id+"F0.imprint","IMPRINT",EDGE,{"derivedFrom":subQ0}),1.0]])]});}
            var Q3;
            {var subQ0=sQuery(id+"F0.wireOp",EDGE,"E181");Q3=makeQuery(id+"F0.imprint","IMPRINT",FACE,{"disambiguationData":[TD([[makeQuery(id+"F0.imprint","IMPRINT",EDGE,{"derivedFrom":subQ0}),1.0]])]});}
            var Q4;
            {var subQ0=sQuery(id+"F0.wireOp",EDGE,"E180");Q4=makeQuery(id+"F0.imprint","IMPRINT",FACE,{"disambiguationData":[TD([[makeQuery(id+"F0.imprint","IMPRINT",EDGE,{"derivedFrom":subQ0}),1.0]])]});}
            var Q5;
            {var subQ0=sQuery(id+"F0.wireOp",EDGE,"E179");Q5=makeQuery(id+"F0.imprint","IMPRINT",FACE,{"disambiguationData":[TD([[makeQuery(id+"F0.imprint","IMPRINT",EDGE,{"derivedFrom":subQ0}),1.0]])]});}
            var Q6;
            {var subQ4=sQuery(id+"F0.wireOp",EDGE,"E282");Q6=makeQuery(id+"F0.imprint","IMPRINT",FACE,{"disambiguationData":[TD([[makeQuery(id+"F0.imprint","IMPRINT",EDGE,{"derivedFrom":subQ4}),-1.0]])]});}
            var Q7;
            {var subQ4=sQuery(id+"F0.wireOp",EDGE,"E160.0");Q7=makeQuery(id+"F0.imprint","IMPRINT",FACE,{"disambiguationData":[TD([[makeQuery(id+"F0.imprint","IMPRINT",EDGE,{"derivedFrom":subQ4}),-1.0]])]});}
            var Q8;
            {var subQ5=sQuery(id+"F0.wireOp",EDGE,"E290");Q8=makeQuery(id+"F0.imprint","IMPRINT",FACE,{"disambiguationData":[TD([[makeQuery(id+"F0.imprint","IMPRINT",EDGE,{"derivedFrom":subQ5}),1.0]])]});}
            var Q9;
            {var subQ5=sQuery(id+"F0.wireOp",EDGE,"E289");Q9=makeQuery(id+"F0.imprint","IMPRINT",FACE,{"disambiguationData":[TD([[makeQuery(id+"F0.imprint","IMPRINT",EDGE,{"derivedFrom":subQ5}),-1.0]])]});}
            var Q10;
            {var subQ5=sQuery(id+"F0.wireOp",EDGE,"E276");Q10=makeQuery(id+"F0.imprint","IMPRINT",FACE,{"disambiguationData":[TD([[makeQuery(id+"F0.imprint","IMPRINT",EDGE,{"derivedFrom":subQ5}),1.0]])]});}
            var Q11;
            {var subQ5=sQuery(id+"F0.wireOp",EDGE,"E277");Q11=makeQuery(id+"F0.imprint","IMPRINT",FACE,{"disambiguationData":[TD([[makeQuery(id+"F0.imprint","IMPRINT",EDGE,{"derivedFrom":subQ5}),-1.0]])]});}
            var Q12;
            {var subQ5=sQuery(id+"F0.wireOp",EDGE,"E286");Q12=makeQuery(id+"F0.imprint","IMPRINT",FACE,{"disambiguationData":[TD([[makeQuery(id+"F0.imprint","IMPRINT",EDGE,{"derivedFrom":subQ5}),-1.0]])]});}
            var Q13;
            {var subQ5=sQuery(id+"F0.wireOp",EDGE,"E278");Q13=makeQuery(id+"F0.imprint","IMPRINT",FACE,{"disambiguationData":[TD([[makeQuery(id+"F0.imprint","IMPRINT",EDGE,{"derivedFrom":subQ5}),-1.0]])]});}
            var Q14;
            {var subQ5=sQuery(id+"F0.wireOp",EDGE,"E279");Q14=makeQuery(id+"F0.imprint","IMPRINT",FACE,{"disambiguationData":[TD([[makeQuery(id+"F0.imprint","IMPRINT",EDGE,{"derivedFrom":subQ5}),-1.0]])]});}
            var Q15;
            {var subQ3=sQuery(id+"F0.wireOp",EDGE,"E287");Q15=makeQuery(id+"F0.imprint","IMPRINT",FACE,{"disambiguationData":[TD([[makeQuery(id+"F0.imprint","IMPRINT",EDGE,{"derivedFrom":subQ3}),-1.0]])]});}
            var Q16;
            {var subQ3=sQuery(id+"F0.wireOp",EDGE,"E288");Q16=makeQuery(id+"F0.imprint","IMPRINT",FACE,{"disambiguationData":[TD([[makeQuery(id+"F0.imprint","IMPRINT",EDGE,{"derivedFrom":subQ3}),-1.0]])]});}
            var Q17;
            {var subQ5=sQuery(id+"F0.wireOp",EDGE,"E280");Q17=makeQuery(id+"F0.imprint","IMPRINT",FACE,{"disambiguationData":[TD([[makeQuery(id+"F0.imprint","IMPRINT",EDGE,{"derivedFrom":subQ5}),-1.0]])]});}
            var Q18;
            {var subQ3=sQuery(id+"F0.wireOp",EDGE,"E281");Q18=makeQuery(id+"F0.imprint","IMPRINT",FACE,{"disambiguationData":[TD([[makeQuery(id+"F0.imprint","IMPRINT",EDGE,{"derivedFrom":subQ3}),-1.0]])]});}
            extrude(context, id + "F8", {"entities" : qUnion([Q0, Q1, Q2, Q3, Q4, Q5, Q6, Q7, Q8, Q9, Q10, Q11, Q12, Q13, Q14, Q15, Q16, Q17, Q18]), "depth" : 25.4 * mm, "offsetDistance" : 25.4 * mm});
        }
        {
            var Q0;
            {var subQ0=sQuery(id+"F0.wireOp",EDGE,"E177");Q0=makeQuery(id+"F0.imprint","IMPRINT",FACE,{"disambiguationData":[TD([[makeQuery(id+"F0.imprint","IMPRINT",EDGE,{"derivedFrom":subQ0}),1.0]])]});}
            var Q1;
            {var subQ0=sQuery(id+"F0.wireOp",EDGE,"E176");Q1=makeQuery(id+"F0.imprint","IMPRINT",FACE,{"disambiguationData":[TD([[makeQuery(id+"F0.imprint","IMPRINT",EDGE,{"derivedFrom":subQ0}),1.0]])]});}
            var Q2;
            {var subQ4=sQuery(id+"F0.wireOp",EDGE,"E289");Q2=makeQuery(id+"F0.imprint","IMPRINT",FACE,{"disambiguationData":[TD([[makeQuery(id+"F0.imprint","IMPRINT",EDGE,{"derivedFrom":subQ4}),1.0]])]});}
            var Q3;
            {var subQ4=sQuery(id+"F0.wireOp",EDGE,"E276");Q3=makeQuery(id+"F0.imprint","IMPRINT",FACE,{"disambiguationData":[TD([[makeQuery(id+"F0.imprint","IMPRINT",EDGE,{"derivedFrom":subQ4}),-1.0]])]});}
            var Q4;
            {var subQ4=sQuery(id+"F0.wireOp",EDGE,"E277");Q4=makeQuery(id+"F0.imprint","IMPRINT",FACE,{"disambiguationData":[TD([[makeQuery(id+"F0.imprint","IMPRINT",EDGE,{"derivedFrom":subQ4}),1.0]])]});}
            var Q5;
            {var subQ2=sQuery(id+"F0.wireOp",EDGE,"E286");Q5=makeQuery(id+"F0.imprint","IMPRINT",FACE,{"disambiguationData":[TD([[makeQuery(id+"F0.imprint","IMPRINT",EDGE,{"derivedFrom":subQ2}),1.0]])]});}
            var Q6;
            {var subQ0=sQuery(id+"F0.wireOp",EDGE,"E272");Q6=makeQuery(id+"F0.imprint","IMPRINT",FACE,{"disambiguationData":[TD([[makeQuery(id+"F0.imprint","IMPRINT",EDGE,{"derivedFrom":subQ0}),1.0]])]});}
            var Q7;
            {var subQ0=sQuery(id+"F0.wireOp",EDGE,"E273");Q7=makeQuery(id+"F0.imprint","IMPRINT",FACE,{"disambiguationData":[TD([[makeQuery(id+"F0.imprint","IMPRINT",EDGE,{"derivedFrom":subQ0}),-1.0]])]});}
            var Q8;
            {var subQ0=sQuery(id+"F0.wireOp",EDGE,"E284");Q8=makeQuery(id+"F0.imprint","IMPRINT",FACE,{"disambiguationData":[TD([[makeQuery(id+"F0.imprint","IMPRINT",EDGE,{"derivedFrom":subQ0}),-1.0]])]});}
            var Q9;
            {var subQ0=sQuery(id+"F0.wireOp",EDGE,"E285");Q9=makeQuery(id+"F0.imprint","IMPRINT",FACE,{"disambiguationData":[TD([[makeQuery(id+"F0.imprint","IMPRINT",EDGE,{"derivedFrom":subQ0}),-1.0]])]});}
            var Q10;
            {var subQ0=sQuery(id+"F0.wireOp",EDGE,"E280");Q10=makeQuery(id+"F0.imprint","IMPRINT",FACE,{"disambiguationData":[TD([[makeQuery(id+"F0.imprint","IMPRINT",EDGE,{"derivedFrom":subQ0}),1.0]])]});}
            var Q11;
            {var subQ0=sQuery(id+"F0.wireOp",EDGE,"E281");Q11=makeQuery(id+"F0.imprint","IMPRINT",FACE,{"disambiguationData":[TD([[makeQuery(id+"F0.imprint","IMPRINT",EDGE,{"derivedFrom":subQ0}),1.0]])]});}
            extrude(context, id + "F9", {"entities" : qUnion([Q0, Q1, Q2, Q3, Q4, Q5, Q6, Q7, Q8, Q9, Q10, Q11]), "depth" : 25.4 * mm, "offsetDistance" : 25.4 * mm});
        }
        {
            var Q0;
            Q0=makeQuery(id+"F0.imprint","IMPRINT",FACE,{"disambiguationData":[TD([[makeQuery(id+"F0.imprint","IMPRINT",EDGE,{"derivedFrom":sQuery(id+"F0.wireOp",EDGE,"E185")}),-1.0]])]});
            extrude(context, id + "F10", {"entities" : qUnion([Q0]), "depth" : 25.4 * mm, "offsetDistance" : 25.4 * mm});
        }
        {
            var Q0;
            {var subQ0=sQuery(id+"F0.wireOp",EDGE,"E188");Q0=makeQuery(id+"F0.imprint","IMPRINT",FACE,{"disambiguationData":[TD([[makeQuery(id+"F0.imprint","IMPRINT",EDGE,{"derivedFrom":subQ0}),1.0]])]});}
            var Q1;
            {var subQ7=sQuery(id+"F0.wireOp",EDGE,"E185");Q1=makeQuery(id+"F0.imprint","IMPRINT",FACE,{"disambiguationData":[TD([[makeQuery(id+"F0.imprint","IMPRINT",EDGE,{"derivedFrom":subQ7}),1.0]])]});}
            var Q2;
            {var subQ0=sQuery(id+"F0.wireOp",EDGE,"E186");Q2=makeQuery(id+"F0.imprint","IMPRINT",FACE,{"disambiguationData":[TD([[makeQuery(id+"F0.imprint","IMPRINT",EDGE,{"derivedFrom":subQ0}),1.0]])]});}
            var Q3;
            {var subQ4=sQuery(id+"F0.wireOp",EDGE,"E187");Q3=makeQuery(id+"F0.imprint","IMPRINT",FACE,{"disambiguationData":[TD([[makeQuery(id+"F0.imprint","IMPRINT",EDGE,{"derivedFrom":subQ4}),1.0]])]});}
            extrude(context, id + "F11", {"entities" : qUnion([Q0, Q1, Q2, Q3]), "depth" : 25.4 * mm, "offsetDistance" : 25.4 * mm});
        }
        {
            var Q0;
            {var subQ0=sQuery(id+"F0.wireOp",EDGE,"E168");Q0=makeQuery(id+"F0.imprint","IMPRINT",FACE,{"disambiguationData":[TD([[makeQuery(id+"F0.imprint","IMPRINT",EDGE,{"derivedFrom":subQ0}),-1.0]])]});}
            var Q1;
            {var subQ0=sQuery(id+"F0.wireOp",EDGE,"E155");Q1=makeQuery(id+"F0.imprint","IMPRINT",FACE,{"disambiguationData":[TD([[makeQuery(id+"F0.imprint","IMPRINT",EDGE,{"derivedFrom":subQ0}),1.0]])]});}
            var Q2;
            {var subQ0=sQuery(id+"F0.wireOp",EDGE,"E157");Q2=makeQuery(id+"F0.imprint","IMPRINT",FACE,{"disambiguationData":[TD([[makeQuery(id+"F0.imprint","IMPRINT",EDGE,{"derivedFrom":subQ0}),-1.0]])]});}
            var Q3;
            {var subQ0=sQuery(id+"F0.wireOp",EDGE,"E171");Q3=makeQuery(id+"F0.imprint","IMPRINT",FACE,{"disambiguationData":[TD([[makeQuery(id+"F0.imprint","IMPRINT",EDGE,{"derivedFrom":subQ0}),-1.0]])]});}
            var Q4;
            {var subQ0=sQuery(id+"F0.wireOp",EDGE,"E158");Q4=makeQuery(id+"F0.imprint","IMPRINT",FACE,{"disambiguationData":[TD([[makeQuery(id+"F0.imprint","IMPRINT",EDGE,{"derivedFrom":subQ0}),-1.0]])]});}
            var Q5;
            {var subQ0=sQuery(id+"F0.wireOp",EDGE,"E152");Q5=makeQuery(id+"F0.imprint","IMPRINT",FACE,{"disambiguationData":[TD([[makeQuery(id+"F0.imprint","IMPRINT",EDGE,{"derivedFrom":subQ0}),-1.0]])]});}
            var Q6;
            {var subQ4=sQuery(id+"F0.wireOp",EDGE,"E149");Q6=makeQuery(id+"F0.imprint","IMPRINT",FACE,{"disambiguationData":[TD([[makeQuery(id+"F0.imprint","IMPRINT",EDGE,{"derivedFrom":subQ4}),1.0]])]});}
            var Q7;
            {var subQ0=sQuery(id+"F0.wireOp",EDGE,"E165");Q7=makeQuery(id+"F0.imprint","IMPRINT",FACE,{"disambiguationData":[TD([[makeQuery(id+"F0.imprint","IMPRINT",EDGE,{"derivedFrom":subQ0}),1.0]])]});}
            var Q8;
            {var subQ4=sQuery(id+"F0.wireOp",EDGE,"E140");Q8=makeQuery(id+"F0.imprint","IMPRINT",FACE,{"disambiguationData":[TD([[makeQuery(id+"F0.imprint","IMPRINT",EDGE,{"derivedFrom":subQ4}),1.0]])]});}
            var Q9;
            {var subQ7=sQuery(id+"F0.wireOp",EDGE,"E143");Q9=makeQuery(id+"F0.imprint","IMPRINT",FACE,{"disambiguationData":[TD([[makeQuery(id+"F0.imprint","IMPRINT",EDGE,{"derivedFrom":subQ7}),1.0]])]});}
            var Q10;
            {var subQ3=sQuery(id+"F0.wireOp",EDGE,"E160.0");Q10=makeQuery(id+"F0.imprint","IMPRINT",FACE,{"disambiguationData":[TD([[makeQuery(id+"F0.imprint","IMPRINT",EDGE,{"derivedFrom":subQ3}),1.0]])]});}
            var Q11;
            {var subQ0=sQuery(id+"F0.wireOp",EDGE,"E159");Q11=makeQuery(id+"F0.imprint","IMPRINT",FACE,{"disambiguationData":[TD([[makeQuery(id+"F0.imprint","IMPRINT",EDGE,{"derivedFrom":subQ0}),-1.0]])]});}
            extrude(context, id + "F12", {"entities" : qUnion([Q0, Q1, Q2, Q3, Q4, Q5, Q6, Q7, Q8, Q9, Q10, Q11]), "depth" : 25.4 * mm, "offsetDistance" : 25.4 * mm});
        }
    });
